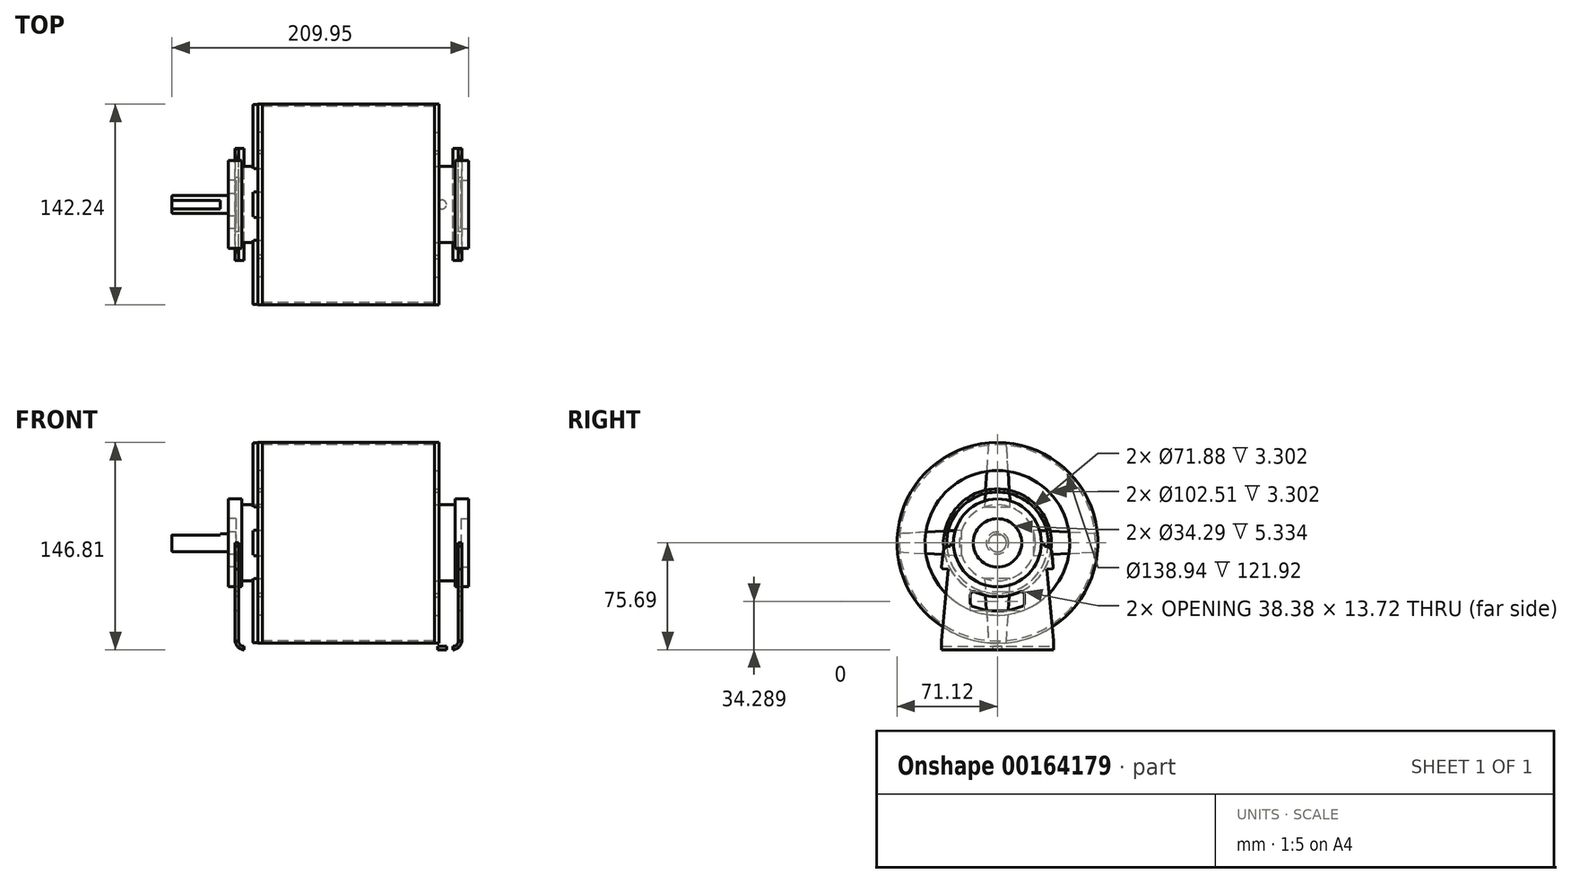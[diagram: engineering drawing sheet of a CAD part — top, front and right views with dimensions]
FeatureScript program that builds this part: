
annotation { "Feature Type Name" : "Feature", "Feature Type Description" : "" }
export const myFeature = defineFeature(function(context is Context, id is Id, definition is map)
    precondition{}
    {
        {
            var Q0;
            Q0=qCreatedBy(makeId("Right.planeOp"),FACE);
            var sketch = newSketch(context, id + "F0", { "sketchPlane" : qUnion([Q0])});
            skCircle(sketch, "E0", {"center": v(0, 0) * mm, "radius": 71.12 * mm});
            skCircle(sketch, "E1.0", {"center": v(0, 0) * mm, "radius": 69.47 * mm});
            skSolve(sketch);
        }
        {
            var Q0;
            Q0=makeQuery(id+"F0.imprint","IMPRINT",FACE,{"disambiguationData":[TD([[makeQuery(id+"F0.imprint","IMPRINT",EDGE,{"derivedFrom":sQuery(id+"F0.wireOp",EDGE,"E0")}),1.0]])]});
            extrude(context, id + "F1", {"entities" : qUnion([Q0]), "depth" : 121.92 * mm});
        }
        {
            var Q0;
            Q0=qCreatedBy(makeId("Front.planeOp"),FACE);
            var sketch = newSketch(context, id + "F2", { "sketchPlane" : qUnion([Q0])});
            skLineSegment(sketch, "E2", {"start": v(0, 0) * mm, "end": v(0, 71.12) * mm});
            skLineSegment(sketch, "E3", {"start": v(0, 71.12) * mm, "end": v(-3.3, 71.12) * mm});
            skLineSegment(sketch, "E4", {"start": v(-3.3, 71.12) * mm, "end": v(-3.3, 26.92) * mm});
            skLineSegment(sketch, "E5", {"start": v(-3.3, 26.92) * mm, "end": v(-14.48, 26.92) * mm});
            skLineSegment(sketch, "E6", {"start": v(-14.48, 26.92) * mm, "end": v(-14.48, 31.12) * mm});
            skLineSegment(sketch, "E7", {"start": v(-14.48, 31.12) * mm, "end": v(-24, 31.12) * mm});
            skLineSegment(sketch, "E8", {"start": v(-24, 31.12) * mm, "end": v(-24, 17.15) * mm});
            skLineSegment(sketch, "E9", {"start": v(-24, 17.15) * mm, "end": v(-18.67, 17.15) * mm});
            skLineSegment(sketch, "E10", {"start": v(-18.67, 17.15) * mm, "end": v(-18.67, 0) * mm});
            skLineSegment(sketch, "E11", {"start": v(-18.67, 0) * mm, "end": v(0, 0) * mm});
            skSolve(sketch);
        }
        {
            var Q0;
            Q0=makeQuery(id+"F2.imprint","IMPRINT",FACE,{"disambiguationData":[TD([[makeQuery(id+"F2.imprint","IMPRINT",EDGE,{"derivedFrom":sQuery(id+"F2.wireOp",EDGE,"E2")}),1.0]])]});
            var Q1;
            Q1=sQuery(id+"F2.wireOp",EDGE,"E11");
            revolve(context, id + "F3", {"entities" : qUnion([Q0]), "axis" : qUnion([Q1]), "revolveType" : RevolveType.FULL});
        }
        {
            var Q0;
            Q0=makeQuery(id+"F3.opRevolve","SWEPT_FACE",FACE,{"disambiguationData":[OSD([sQuery(id+"F2.wireOp",EDGE,"E4")])]});
            var sketch = newSketch(context, id + "F4", { "sketchPlane" : qUnion([Q0])});
            skCircle(sketch, "E12", {"center": v(0, 0) * mm, "radius": 51.26 * mm});
            skCircle(sketch, "E13", {"center": v(0, 0) * mm, "radius": 38.23 * mm});
            skCircle(sketch, "E14.0", {"center": v(0, 0) * mm, "radius": 35.94 * mm});
            skSolve(sketch);
        }
        {
            var Q0;
            Q0=qSketchRegion(id+"F4",true);
            var Q1;
            Q1=makeQuery(id+"F4.imprint","IMPRINT",FACE,{"disambiguationData":[TD([[makeQuery(id+"F4.imprint","IMPRINT",EDGE,{"derivedFrom":sQuery(id+"F4.wireOp",EDGE,"E14.0")}),1.0]])]});
            extrude(context, id + "F5", {"entities" : qUnion([Q0, Q1]), "operationType" : NewBodyOperationType.REMOVE, "endBound" : BoundingType.THROUGH_ALL, "oppositeDirection" : true, "depth" : 25.4 * mm});
        }
        {
            var Q0;
            Q0=qCreatedBy(makeId("Right.planeOp"),FACE);
            var sketch = newSketch(context, id + "F6", { "sketchPlane" : qUnion([Q0])});
            skLineSegment(sketch, "E15", {"start": v(0, 0) * mm, "end": v(0, 71.12) * mm, "construction": true});
            skPoint(sketch, "E16.rect.middle", {"position": v(0, 71.12) * mm});
            skCircle(sketch, "E17", {"center": v(0, 26.92) * mm, "radius": 9.2 * mm, "construction": true});
            skCircle(sketch, "E18.0", {"center": v(0, 0) * mm, "radius": 71.12 * mm, "construction": true});
            skCircle(sketch, "E19", {"center": v(0, 71.12) * mm, "radius": 6.35 * mm, "construction": true});
            skLineSegment(sketch, "E20", {"start": v(9.07, 25.35) * mm, "end": v(6.38, 70.83) * mm});
            skLineSegment(sketch, "E21", {"start": v(6.38, 70.83) * mm, "end": v(-6.38, 70.83) * mm});
            skLineSegment(sketch, "E22", {"start": v(-6.38, 70.83) * mm, "end": v(-9.07, 25.35) * mm});
            skLineSegment(sketch, "E23", {"start": v(-9.07, 25.35) * mm, "end": v(9.07, 25.35) * mm});
            skCircle(sketch, "E24.0", {"center": v(0, 0) * mm, "radius": 26.92 * mm, "construction": true});
            skSolve(sketch);
        }
        {
            var Q0;
            {var subQ3=sQuery(id+"F6.wireOp",EDGE,"E20");Q0=makeQuery(id+"F6.imprint","IMPRINT",FACE,{"disambiguationData":[TD([[makeQuery(id+"F6.imprint","IMPRINT",EDGE,{"derivedFrom":subQ3}),1.0]])]});}
            extrude(context, id + "F7", {"entities" : qUnion([Q0]), "oppositeDirection" : true, "depth" : 6.6 * mm});
        }
        {
            var Q0;
            Q0=makeQuery(id+"F7.opExtrude","CAP_EDGE",EDGE,{"disambiguationData":[OSD([sQuery(id+"F6.wireOp",EDGE,"E20")])],"isStart":false});
            var Q1;
            Q1=makeQuery(id+"F7.opExtrude","CAP_EDGE",EDGE,{"disambiguationData":[OSD([sQuery(id+"F6.wireOp",EDGE,"E21")])],"isStart":false});
            var Q2;
            Q2=makeQuery(id+"F7.opExtrude","CAP_EDGE",EDGE,{"disambiguationData":[OSD([sQuery(id+"F6.wireOp",EDGE,"E22")])],"isStart":false});
            var Q3;
            Q3=makeQuery(id+"F7.opExtrude","SWEPT_EDGE",EDGE,{"disambiguationData":[OSD([sQuery(id+"F2.wireOp",EDGE,"E3"),sQuery(id+"F2.wireOp",EDGE,"E4"),sQuery(id+"F6.wireOp",EDGE,"E20"),sQuery(id+"F6.wireOp",EDGE,"E21")])]});
            var Q4;
            Q4=makeQuery(id+"F7.opExtrude","SWEPT_EDGE",EDGE,{"disambiguationData":[OSD([sQuery(id+"F2.wireOp",EDGE,"E3"),sQuery(id+"F2.wireOp",EDGE,"E4"),sQuery(id+"F6.wireOp",EDGE,"E21"),sQuery(id+"F6.wireOp",EDGE,"E22")])]});
            fillet(context, id + "F8", {"entities" : qUnion([Q0, Q1, Q2, Q3, Q4]), "radius" : 0.5 * mm, "tangentPropagation" : true, "allowEdgeOverflow" : false});
        }
        {
            var Q0;
            Q0=makeQuery(id+"F7.opExtrude","SWEPT_BODY",BODY,{"disambiguationData":[OSD([sQuery(id+"F2.wireOp",EDGE,"E4"),sQuery(id+"F2.wireOp",EDGE,"E5"),sQuery(id+"F6.wireOp",EDGE,"E20"),sQuery(id+"F6.wireOp",EDGE,"E21"),sQuery(id+"F6.wireOp",EDGE,"E22")])]});
            var Q1;
            Q1=sQuery(id+"F2.wireOp",EDGE,"E11");
            circularPattern(context, id + "F9", {"entities" : qUnion([Q0]), "axis" : qUnion([Q1]), "angle" : 360 * degree, "instanceCount" : 4, "equalSpace" : true});
        }
        {
            var Q0;
            Q0=qCreatedBy(makeId("Right.planeOp"),FACE);
            cPlane(context, id + "F10", {"entities" : qUnion([Q0]), "cplaneType" : CPlaneType.OFFSET, "offset" : 60.96 * mm, "width" : 152.4 * mm, "height" : 152.4 * mm});
        }
        {
            var Q0;
            Q0=makeQuery(id+"F5.boolean.opBoolean","SPLIT",BODY,{"disambiguationData":[OD(0.0)],"derivedFrom":makeQuery(id+"F3.opRevolve","SWEPT_BODY",BODY,{"disambiguationData":[OSD([sQuery(id+"F2.wireOp",EDGE,"E2"),sQuery(id+"F2.wireOp",EDGE,"E3"),sQuery(id+"F2.wireOp",EDGE,"E4"),sQuery(id+"F2.wireOp",EDGE,"E5"),sQuery(id+"F2.wireOp",EDGE,"E6"),sQuery(id+"F2.wireOp",EDGE,"E7"),sQuery(id+"F2.wireOp",EDGE,"E8"),sQuery(id+"F2.wireOp",EDGE,"E9"),sQuery(id+"F2.wireOp",EDGE,"E10"),sQuery(id+"F2.wireOp",EDGE,"E11")])]})});
            var Q1;
            Q1=qCreatedBy(id+"F10.planeOp",FACE);
            mirror(context, id + "F11", {"entities" : qUnion([Q0]), "mirrorPlane" : qUnion([Q1])});
        }
        {
            var Q0;
            Q0=qCreatedBy(makeId("Front.planeOp"),FACE);
            var sketch = newSketch(context, id + "F12", { "sketchPlane" : qUnion([Q0])});
            skLineSegment(sketch, "E25.0.0", {"start": v(-18.67, -17.15) * mm, "end": v(-18.67, 17.15) * mm, "construction": true});
            skLineSegment(sketch, "E26", {"start": v(-18.67, 0) * mm, "end": v(-64.03, 0) * mm});
            skLineSegment(sketch, "E27", {"start": v(-64.03, 0) * mm, "end": v(-64.03, 5.84) * mm});
            skLineSegment(sketch, "E28", {"start": v(-63.53, 6.35) * mm, "end": v(-23.75, 6.35) * mm});
            skLineSegment(sketch, "E29", {"start": v(-23.24, 7.89) * mm, "end": v(-18.67, 7.89) * mm});
            skLineSegment(sketch, "E30", {"start": v(-18.67, 7.89) * mm, "end": v(-18.67, 0) * mm});
            skLineSegment(sketch, "E31", {"start": v(-23.75, 7.38) * mm, "end": v(-23.75, 6.35) * mm});
            skPoint(sketch, "E32.visualSharp", {"position": v(-23.75, 7.89) * mm});
            skArc(sketch, "E32.filletArc", {"start": v(-23.24, 7.89) * mm, "mid": v(-23.6, 7.74) * mm, "end": v(-23.75, 7.38) * mm});
            skPoint(sketch, "E33.visualSharp", {"position": v(-64.03, 6.35) * mm});
            skArc(sketch, "E33.filletArc", {"start": v(-63.53, 6.35) * mm, "mid": v(-63.88, 6.2) * mm, "end": v(-64.03, 5.84) * mm});
            skSolve(sketch);
        }
        {
            var Q0;
            Q0=makeQuery(id+"F12.imprint","IMPRINT",FACE,{"disambiguationData":[TD([[makeQuery(id+"F12.imprint","IMPRINT",EDGE,{"derivedFrom":sQuery(id+"F12.wireOp",EDGE,"E26")}),-1.0]])]});
            var Q1;
            Q1=sQuery(id+"F12.wireOp",EDGE,"E26");
            revolve(context, id + "F13", {"entities" : qUnion([Q0]), "axis" : qUnion([Q1]), "revolveType" : RevolveType.FULL});
        }
        {
            var Q0;
            Q0=makeQuery(id+"F13.opRevolve","SWEPT_FACE",FACE,{"disambiguationData":[OSD([sQuery(id+"F12.wireOp",EDGE,"E27")])]});
            var sketch = newSketch(context, id + "F14", { "sketchPlane" : qUnion([Q0])});
            skCircle(sketch, "E34.0", {"center": v(0, 0) * mm, "radius": 6.35 * mm});
            skLineSegment(sketch, "E35", {"start": v(-6.6, -6.35) * mm, "end": v(6.6, -6.35) * mm, "construction": true});
            skLineSegment(sketch, "E36", {"start": v(0, -6.35) * mm, "end": v(0, 6.35) * mm, "construction": true});
            skLineSegment(sketch, "E37.0", {"start": v(-3.02, 5.59) * mm, "end": v(3.02, 5.59) * mm});
            skSolve(sketch);
        }
        {
            var Q0;
            {var subQ0=makeQuery(id+"F13.opRevolve","SWEPT_EDGE",EDGE,{"disambiguationData":[OSD([sQuery(id+"F12.wireOp",EDGE,"E27"),sQuery(id+"F12.wireOp",EDGE,"E33.filletArc")])]});var subQ1=sQuery(id+"F14.wireOp",EDGE,"E37.0");var subQ3=makeQuery(id+"F14.imprint","INTERSECT",VERTEX,{"disambiguationData":[OD(0.0)],"derivedFrom":[subQ0,subQ1]});Q0=makeQuery(id+"F14.imprint","IMPRINT",FACE,{"disambiguationData":[TD([[makeQuery(id+"F14.imprint","IMPRINT",EDGE,{"disambiguationData":[TD([[subQ3,-1.0]])],"derivedFrom":subQ1}),1.0]])]});}
            var Q1;
            {var subQ1=sQuery(id+"F14.wireOp",EDGE,"E37.0");var subQ4=sQuery(id+"F14.wireOp",EDGE,"E34.0");var subQ6=makeQuery(id+"F14.imprint","INTERSECT",VERTEX,{"disambiguationData":[OD(0.0)],"derivedFrom":[subQ4,subQ1]});Q1=makeQuery(id+"F14.imprint","IMPRINT",FACE,{"disambiguationData":[TD([[makeQuery(id+"F14.imprint","IMPRINT",EDGE,{"disambiguationData":[TD([[subQ6,1.0]])],"derivedFrom":subQ4}),1.0]])]});}
            extrude(context, id + "F15", {"entities" : qUnion([Q0, Q1]), "operationType" : NewBodyOperationType.REMOVE, "oppositeDirection" : true, "depth" : 34.04 * mm});
        }
        {
            var Q0;
            Q0=qCreatedBy(makeId("Front.planeOp"),FACE);
            var sketch = newSketch(context, id + "F16", { "sketchPlane" : qUnion([Q0])});
            skLineSegment(sketch, "E38", {"start": v(-154.25, 0) * mm, "end": v(252.33, 0) * mm, "construction": true});
            skLineSegment(sketch, "E39", {"start": v(-12.9, -75.7) * mm, "end": v(134.81, -75.7) * mm});
            skLineSegment(sketch, "E40", {"start": v(-24, 31.12) * mm, "end": v(-14.48, 31.12) * mm, "construction": true});
            skLineSegment(sketch, "E41", {"start": v(136.4, 31.12) * mm, "end": v(145.92, 31.12) * mm, "construction": true});
            skLineSegment(sketch, "E42", {"start": v(-19.24, 31.12) * mm, "end": v(-19.24, 0) * mm, "construction": true});
            skLineSegment(sketch, "E43", {"start": v(141.16, 31.12) * mm, "end": v(141.16, 0) * mm, "construction": true});
            skLineSegment(sketch, "E44", {"start": v(-19.24, 0) * mm, "end": v(-19.24, -69.34) * mm});
            skLineSegment(sketch, "E45", {"start": v(141.16, 0) * mm, "end": v(141.16, -69.34) * mm});
            skPoint(sketch, "E46.visualSharp", {"position": v(-19.24, -75.7) * mm});
            skArc(sketch, "E46.filletArc", {"start": v(-19.24, -69.34) * mm, "mid": v(-17.38, -73.83) * mm, "end": v(-12.9, -75.7) * mm});
            skPoint(sketch, "E47.visualSharp", {"position": v(141.16, -75.7) * mm});
            skArc(sketch, "E47.filletArc", {"start": v(134.81, -75.7) * mm, "mid": v(139.3, -73.83) * mm, "end": v(141.16, -69.34) * mm});
            skLineSegment(sketch, "E48.0", {"start": v(138.87, 0) * mm, "end": v(138.87, -69.34) * mm});
            skArc(sketch, "E48.1", {"start": v(134.81, -73.4) * mm, "mid": v(137.68, -72.22) * mm, "end": v(138.87, -69.34) * mm});
            skLineSegment(sketch, "E48.2", {"start": v(-12.9, -73.4) * mm, "end": v(134.81, -73.4) * mm});
            skArc(sketch, "E48.3", {"start": v(-16.95, -69.34) * mm, "mid": v(-15.76, -72.22) * mm, "end": v(-12.9, -73.4) * mm});
            skLineSegment(sketch, "E48.4", {"start": v(-16.95, 0) * mm, "end": v(-16.95, -69.34) * mm});
            skLineSegment(sketch, "E49", {"start": v(-19.24, 0) * mm, "end": v(-16.95, 0) * mm});
            skLineSegment(sketch, "E50", {"start": v(138.87, 0) * mm, "end": v(141.16, 0) * mm});
            skSolve(sketch);
        }
        {
            var Q0;
            Q0=qSketchRegion(id+"F16",true);
            extrude(context, id + "F17", {"entities" : qUnion([Q0]), "depth" : 79.5 * mm, "symmetric" : true});
        }
        {
            var Q0;
            Q0=qCreatedBy(makeId("Top.planeOp"),FACE);
            cPlane(context, id + "F18", {"entities" : qUnion([Q0]), "cplaneType" : CPlaneType.OFFSET, "offset" : 75.7 * mm, "oppositeDirection" : true, "width" : 152.4 * mm, "height" : 152.4 * mm});
        }
        {
            var Q0;
            Q0=qCreatedBy(id+"F18.planeOp",FACE);
            var sketch = newSketch(context, id + "F19", { "sketchPlane" : qUnion([Q0])});
            skLineSegment(sketch, "E51.0", {"start": v(-19.24, -39.75) * mm, "end": v(-12.9, -39.75) * mm, "construction": true});
            skLineSegment(sketch, "E52.0", {"start": v(-19.24, 39.75) * mm, "end": v(-12.9, 39.75) * mm, "construction": true});
            skLineSegment(sketch, "E53.bottom", {"start": v(15.34, 66.04) * mm, "end": v(15.34, 66.04) * mm});
            skLineSegment(sketch, "E53.top", {"start": v(15.34, 40.64) * mm, "end": v(15.34, 40.64) * mm});
            skLineSegment(sketch, "E53.left", {"start": v(11.37, 62.07) * mm, "end": v(11.37, 44.6) * mm});
            skLineSegment(sketch, "E53.right", {"start": v(19.3, 62.07) * mm, "end": v(19.3, 44.6) * mm});
            skPoint(sketch, "E54.visualSharp", {"position": v(11.37, 66.04) * mm});
            skArc(sketch, "E54.filletArc", {"start": v(15.34, 66.04) * mm, "mid": v(12.53, 64.88) * mm, "end": v(11.37, 62.07) * mm});
            skPoint(sketch, "E55.visualSharp", {"position": v(19.3, 66.04) * mm});
            skArc(sketch, "E55.filletArc", {"start": v(19.3, 62.07) * mm, "mid": v(18.14, 64.88) * mm, "end": v(15.34, 66.04) * mm});
            skPoint(sketch, "E56.visualSharp", {"position": v(19.3, 40.64) * mm});
            skArc(sketch, "E56.filletArc", {"start": v(15.34, 40.64) * mm, "mid": v(18.14, 41.8) * mm, "end": v(19.3, 44.6) * mm});
            skPoint(sketch, "E57.visualSharp", {"position": v(11.37, 40.64) * mm});
            skArc(sketch, "E57.filletArc", {"start": v(11.37, 44.6) * mm, "mid": v(12.53, 41.8) * mm, "end": v(15.34, 40.64) * mm});
            skLineSegment(sketch, "E58", {"start": v(2.98, 39.75) * mm, "end": v(2.98, -39.75) * mm, "construction": true});
            skLineSegment(sketch, "E59", {"start": v(-19.24, 0) * mm, "end": v(141.16, 0) * mm, "construction": true});
            skLineSegment(sketch, "E60", {"start": v(9.33, 71.5) * mm, "end": v(111.68, 71.5) * mm});
            skLineSegment(sketch, "E61", {"start": v(9.33, -71.5) * mm, "end": v(111.68, -71.5) * mm});
            skLineSegment(sketch, "E62", {"start": v(2.98, 46.1) * mm, "end": v(2.98, 65.15) * mm});
            skLineSegment(sketch, "E63", {"start": v(2.98, -46.1) * mm, "end": v(2.98, -65.15) * mm});
            skLineSegment(sketch, "E64", {"start": v(-19.24, 39.75) * mm, "end": v(-19.24, -39.75) * mm, "construction": true});
            skLineSegment(sketch, "E65.0", {"start": v(141.16, -39.75) * mm, "end": v(141.16, 39.75) * mm, "construction": true});
            skLineSegment(sketch, "E66", {"start": v(141.16, 39.75) * mm, "end": v(134.81, 39.75) * mm, "construction": true});
            skLineSegment(sketch, "E67", {"start": v(126.25, 45.4) * mm, "end": v(117.6, 67.47) * mm});
            skPoint(sketch, "E68.visualSharp", {"position": v(128.46, 39.75) * mm});
            skArc(sketch, "E68.filletArc", {"start": v(126.25, 45.4) * mm, "mid": v(129.51, 41.3) * mm, "end": v(134.52, 39.75) * mm});
            skPoint(sketch, "E69.visualSharp", {"position": v(2.98, 71.5) * mm});
            skArc(sketch, "E69.filletArc", {"start": v(9.33, 71.5) * mm, "mid": v(4.84, 69.64) * mm, "end": v(2.98, 65.15) * mm});
            skLineSegment(sketch, "E70.0.MirrorCS", {"start": v(141.16, -39.75) * mm, "end": v(134.81, -39.75) * mm, "construction": true});
            skLineSegment(sketch, "E70.1.MirrorCS", {"start": v(126.25, -45.4) * mm, "end": v(117.6, -67.47) * mm});
            skArc(sketch, "E70.2.MirrorCS", {"start": v(126.25, -45.4) * mm, "mid": v(129.51, -41.3) * mm, "end": v(134.52, -39.75) * mm});
            skPoint(sketch, "E71.visualSharp", {"position": v(116.01, 71.5) * mm});
            skArc(sketch, "E71.filletArc", {"start": v(117.6, 67.47) * mm, "mid": v(115.26, 70.4) * mm, "end": v(111.68, 71.5) * mm});
            skPoint(sketch, "E72.visualSharp", {"position": v(116.01, -71.5) * mm});
            skArc(sketch, "E72.filletArc", {"start": v(111.68, -71.5) * mm, "mid": v(115.26, -70.4) * mm, "end": v(117.6, -67.47) * mm});
            skPoint(sketch, "E73.visualSharp", {"position": v(2.98, -71.5) * mm});
            skArc(sketch, "E73.filletArc", {"start": v(2.98, -65.15) * mm, "mid": v(4.84, -69.64) * mm, "end": v(9.33, -71.5) * mm});
            skPoint(sketch, "E74.visualSharp", {"position": v(2.98, 39.75) * mm});
            skArc(sketch, "E74.filletArc", {"start": v(-3.37, 39.75) * mm, "mid": v(1.12, 41.61) * mm, "end": v(2.98, 46.1) * mm});
            skPoint(sketch, "E75.visualSharp", {"position": v(2.98, -39.75) * mm});
            skArc(sketch, "E75.filletArc", {"start": v(2.98, -46.1) * mm, "mid": v(1.12, -41.61) * mm, "end": v(-3.37, -39.75) * mm});
            skArc(sketch, "E76.0.1.0", {"start": v(15.34, -66.04) * mm, "mid": v(18.14, -64.88) * mm, "end": v(19.3, -62.07) * mm});
            skArc(sketch, "E76.0.1.1", {"start": v(11.37, -62.07) * mm, "mid": v(12.53, -64.88) * mm, "end": v(15.34, -66.04) * mm});
            skLineSegment(sketch, "E76.0.1.2", {"start": v(11.37, -44.6) * mm, "end": v(11.37, -62.07) * mm});
            skArc(sketch, "E76.0.1.3", {"start": v(15.34, -40.64) * mm, "mid": v(12.53, -41.8) * mm, "end": v(11.37, -44.6) * mm});
            skArc(sketch, "E76.0.1.4", {"start": v(19.3, -44.6) * mm, "mid": v(18.14, -41.8) * mm, "end": v(15.34, -40.64) * mm});
            skLineSegment(sketch, "E76.0.1.5", {"start": v(19.3, -44.6) * mm, "end": v(19.3, -62.07) * mm});
            skArc(sketch, "E76.1.0.0", {"start": v(83.92, 40.64) * mm, "mid": v(86.72, 41.8) * mm, "end": v(87.88, 44.6) * mm});
            skArc(sketch, "E76.1.0.1", {"start": v(79.95, 44.6) * mm, "mid": v(81.1, 41.8) * mm, "end": v(83.92, 40.64) * mm});
            skLineSegment(sketch, "E76.1.0.2", {"start": v(79.95, 62.07) * mm, "end": v(79.95, 44.6) * mm});
            skArc(sketch, "E76.1.0.3", {"start": v(83.92, 66.04) * mm, "mid": v(81.1, 64.88) * mm, "end": v(79.95, 62.07) * mm});
            skArc(sketch, "E76.1.0.4", {"start": v(87.88, 62.07) * mm, "mid": v(86.72, 64.88) * mm, "end": v(83.92, 66.04) * mm});
            skLineSegment(sketch, "E76.1.0.5", {"start": v(87.88, 62.07) * mm, "end": v(87.88, 44.6) * mm});
            skArc(sketch, "E76.1.1.0", {"start": v(83.92, -66.04) * mm, "mid": v(86.72, -64.88) * mm, "end": v(87.88, -62.07) * mm});
            skArc(sketch, "E76.1.1.1", {"start": v(79.95, -62.07) * mm, "mid": v(81.1, -64.88) * mm, "end": v(83.92, -66.04) * mm});
            skLineSegment(sketch, "E76.1.1.2", {"start": v(79.95, -44.6) * mm, "end": v(79.95, -62.07) * mm});
            skArc(sketch, "E76.1.1.3", {"start": v(83.92, -40.64) * mm, "mid": v(81.1, -41.8) * mm, "end": v(79.95, -44.6) * mm});
            skArc(sketch, "E76.1.1.4", {"start": v(87.88, -44.6) * mm, "mid": v(86.72, -41.8) * mm, "end": v(83.92, -40.64) * mm});
            skLineSegment(sketch, "E76.1.1.5", {"start": v(87.88, -44.6) * mm, "end": v(87.88, -62.07) * mm});
            skLineSegment(sketch, "E76.direction1", {"start": v(15.34, 40.64) * mm, "end": v(83.92, 40.64) * mm, "construction": true});
            skLineSegment(sketch, "E76.direction2", {"start": v(15.34, 40.64) * mm, "end": v(15.34, -66.04) * mm, "construction": true});
            skLineSegment(sketch, "E77.0", {"start": v(-12.9, -39.75) * mm, "end": v(-12.9, 39.75) * mm});
            skLineSegment(sketch, "E78.0", {"start": v(134.81, -39.75) * mm, "end": v(134.81, 39.75) * mm});
            skLineSegment(sketch, "E79", {"start": v(-12.9, 39.75) * mm, "end": v(-3.37, 39.75) * mm});
            skLineSegment(sketch, "E80", {"start": v(-12.9, -39.75) * mm, "end": v(-3.37, -39.75) * mm});
            skLineSegment(sketch, "E81", {"start": v(134.81, 39.75) * mm, "end": v(134.52, 39.75) * mm});
            skLineSegment(sketch, "E82", {"start": v(134.81, -39.75) * mm, "end": v(134.52, -39.75) * mm});
            skSolve(sketch);
        }
        {
            var Q0;
            Q0=makeQuery(id+"F19.imprint","IMPRINT",FACE,{"disambiguationData":[TD([[makeQuery(id+"F19.imprint","IMPRINT",EDGE,{"derivedFrom":sQuery(id+"F19.wireOp",EDGE,"E53.left")}),-1.0]])]});
            extrude(context, id + "F20", {"entities" : qUnion([Q0]), "operationType" : NewBodyOperationType.ADD, "depth" : 2.3 * mm});
        }
        {
            var Q0;
            Q0=makeQuery(id+"F17.opExtrude","SWEPT_FACE",FACE,{"disambiguationData":[OSD([sQuery(id+"F16.wireOp",EDGE,"E44")])]});
            var sketch = newSketch(context, id + "F21", { "sketchPlane" : qUnion([Q0])});
            skArc(sketch, "E83.0", {"start": v(-31.12, 0) * mm, "mid": v(0, -31.12) * mm, "end": v(31.12, 0) * mm});
            skLineSegment(sketch, "E84.0", {"start": v(39.75, -69.34) * mm, "end": v(-39.75, -69.34) * mm});
            skLineSegment(sketch, "E85", {"start": v(31.87, 0) * mm, "end": v(31.12, 0) * mm});
            skLineSegment(sketch, "E86", {"start": v(-33.13, -1.15) * mm, "end": v(-39.75, -69.34) * mm});
            skLineSegment(sketch, "E87", {"start": v(33.13, -1.15) * mm, "end": v(39.75, -69.34) * mm});
            skPoint(sketch, "E88.end.orphan", {"position": v(-39.75, 0) * mm});
            skPoint(sketch, "E89.0.start.orphan", {"position": v(39.75, 0) * mm});
            skLineSegment(sketch, "E90.trimOffspring", {"start": v(-31.12, 0) * mm, "end": v(-31.87, 0) * mm});
            skLineSegment(sketch, "E91", {"start": v(0, 0) * mm, "end": v(0, -69.34) * mm, "construction": true});
            skPoint(sketch, "E92.visualSharp", {"position": v(-33.02, 0) * mm});
            skArc(sketch, "E92.filletArc", {"start": v(-31.87, 0) * mm, "mid": v(-32.72, -0.33) * mm, "end": v(-33.13, -1.15) * mm});
            skPoint(sketch, "E93.visualSharp", {"position": v(33.02, 0) * mm});
            skArc(sketch, "E93.filletArc", {"start": v(33.13, -1.15) * mm, "mid": v(32.72, -0.33) * mm, "end": v(31.87, 0) * mm});
            skLineSegment(sketch, "E94.bottom", {"start": v(33.27, -2.6) * mm, "end": v(33.78, -2.55) * mm});
            skLineSegment(sketch, "E94.top", {"start": v(34.84, -18.78) * mm, "end": v(38.38, -18.44) * mm});
            skLineSegment(sketch, "E94.left", {"start": v(33.27, -2.6) * mm, "end": v(34.84, -18.78) * mm});
            skLineSegment(sketch, "E94.right", {"start": v(38.5, -6.43) * mm, "end": v(39.52, -17.05) * mm});
            skPoint(sketch, "E95.visualSharp", {"position": v(38.08, -2.13) * mm});
            skArc(sketch, "E95.filletArc", {"start": v(38.5, -6.43) * mm, "mid": v(36.94, -3.51) * mm, "end": v(33.78, -2.55) * mm});
            skPoint(sketch, "E96.visualSharp", {"position": v(39.65, -18.31) * mm});
            skArc(sketch, "E96.filletArc", {"start": v(38.38, -18.44) * mm, "mid": v(39.24, -17.98) * mm, "end": v(39.52, -17.05) * mm});
            skLineSegment(sketch, "E97.0.MirrorCS", {"start": v(-33.27, -2.6) * mm, "end": v(-33.78, -2.55) * mm});
            skArc(sketch, "E97.1.MirrorCS", {"start": v(-38.5, -6.43) * mm, "mid": v(-36.94, -3.51) * mm, "end": v(-33.78, -2.55) * mm});
            skLineSegment(sketch, "E97.2.MirrorCS", {"start": v(-34.84, -18.78) * mm, "end": v(-38.38, -18.44) * mm});
            skLineSegment(sketch, "E97.3.MirrorCS", {"start": v(-38.5, -6.43) * mm, "end": v(-39.52, -17.05) * mm});
            skArc(sketch, "E97.4.MirrorCS", {"start": v(-38.38, -18.44) * mm, "mid": v(-39.24, -17.98) * mm, "end": v(-39.52, -17.05) * mm});
            skArc(sketch, "E98", {"start": v(-15.6, -34.76) * mm, "mid": v(0, -38.1) * mm, "end": v(15.6, -34.76) * mm});
            skArc(sketch, "E99.0", {"start": v(-17.57, -44.95) * mm, "mid": v(0, -48.26) * mm, "end": v(17.57, -44.95) * mm});
            skLineSegment(sketch, "E100.rect.left", {"start": v(19.19, -37.07) * mm, "end": v(19.19, -42.58) * mm});
            skLineSegment(sketch, "E100.rect.right", {"start": v(-19.19, -37.07) * mm, "end": v(-19.19, -42.58) * mm});
            skPoint(sketch, "E100.rect.middle", {"position": v(0, -43.18) * mm});
            skPoint(sketch, "E101.orphan", {"position": v(-19.19, -53.44) * mm});
            skPoint(sketch, "E100.rect.top.start.orphan", {"position": v(19.19, -53.44) * mm});
            skPoint(sketch, "E102.visualSharp", {"position": v(-19.19, -44.28) * mm});
            skArc(sketch, "E102.filletArc", {"start": v(-19.19, -42.58) * mm, "mid": v(-18.75, -44.01) * mm, "end": v(-17.57, -44.95) * mm});
            skPoint(sketch, "E103.visualSharp", {"position": v(19.19, -44.28) * mm});
            skArc(sketch, "E103.filletArc", {"start": v(17.57, -44.95) * mm, "mid": v(18.75, -44.01) * mm, "end": v(19.19, -42.58) * mm});
            skPoint(sketch, "E104.visualSharp", {"position": v(19.19, -32.92) * mm});
            skArc(sketch, "E104.filletArc", {"start": v(19.19, -37.07) * mm, "mid": v(18.03, -34.94) * mm, "end": v(15.6, -34.76) * mm});
            skPoint(sketch, "E105.visualSharp", {"position": v(-19.19, -32.92) * mm});
            skArc(sketch, "E105.filletArc", {"start": v(-15.6, -34.76) * mm, "mid": v(-18.03, -34.94) * mm, "end": v(-19.19, -37.07) * mm});
            skSolve(sketch);
        }
        {
            var Q0;
            {var subQ2=sQuery(id+"F21.wireOp",EDGE,"E92.filletArc");Q0=makeQuery(id+"F21.imprint","IMPRINT",FACE,{"disambiguationData":[TD([[makeQuery(id+"F21.imprint","IMPRINT",EDGE,{"derivedFrom":subQ2}),-1.0]])]});}
            var Q1;
            {var subQ2=sQuery(id+"F21.wireOp",EDGE,"E93.filletArc");Q1=makeQuery(id+"F21.imprint","IMPRINT",FACE,{"disambiguationData":[TD([[makeQuery(id+"F21.imprint","IMPRINT",EDGE,{"derivedFrom":subQ2}),-1.0]])]});}
            var Q2;
            {var subQ1=sQuery(id+"F21.wireOp",EDGE,"E83.0");Q2=makeQuery(id+"F21.imprint","IMPRINT",FACE,{"disambiguationData":[TD([[makeQuery(id+"F21.imprint","IMPRINT",EDGE,{"derivedFrom":subQ1}),1.0]])]});}
            var Q3;
            Q3=makeQuery(id+"F21.imprint","IMPRINT",FACE,{"disambiguationData":[TD([[makeQuery(id+"F21.imprint","IMPRINT",EDGE,{"derivedFrom":sQuery(id+"F21.wireOp",EDGE,"E98")}),-1.0]])]});
            extrude(context, id + "F22", {"entities" : qUnion([Q0, Q1, Q2, Q3]), "oppositeDirection" : true, "depth" : 160.4 * mm});
        }
        {
            var Q0;
            Q0=makeQuery(id+"F22.opExtrude","SWEPT_BODY",BODY,{"disambiguationData":[OSD([sQuery(id+"F16.wireOp",EDGE,"E44"),sQuery(id+"F16.wireOp",EDGE,"E49"),sQuery(id+"F21.wireOp",EDGE,"E83.0")])]});
            var Q1;
            Q1=makeQuery(id+"F22.opExtrude","SWEPT_BODY",BODY,{"disambiguationData":[OSD([sQuery(id+"F16.wireOp",EDGE,"E44"),sQuery(id+"F16.wireOp",EDGE,"E49"),sQuery(id+"F21.wireOp",EDGE,"E86"),sQuery(id+"F21.wireOp",EDGE,"E92.filletArc"),sQuery(id+"F21.wireOp",EDGE,"E97.0.MirrorCS"),sQuery(id+"F21.wireOp",EDGE,"E97.1.MirrorCS"),sQuery(id+"F21.wireOp",EDGE,"E97.2.MirrorCS"),sQuery(id+"F21.wireOp",EDGE,"E97.3.MirrorCS"),sQuery(id+"F21.wireOp",EDGE,"E97.4.MirrorCS")])]});
            var Q2;
            Q2=makeQuery(id+"F22.opExtrude","SWEPT_BODY",BODY,{"disambiguationData":[OSD([sQuery(id+"F16.wireOp",EDGE,"E44"),sQuery(id+"F16.wireOp",EDGE,"E49"),sQuery(id+"F21.wireOp",EDGE,"E87"),sQuery(id+"F21.wireOp",EDGE,"E93.filletArc"),sQuery(id+"F21.wireOp",EDGE,"E94.bottom"),sQuery(id+"F21.wireOp",EDGE,"E94.top"),sQuery(id+"F21.wireOp",EDGE,"E94.right"),sQuery(id+"F21.wireOp",EDGE,"E95.filletArc"),sQuery(id+"F21.wireOp",EDGE,"E96.filletArc")])]});
            var Q3;
            Q3=makeQuery(id+"F22.opExtrude","SWEPT_BODY",BODY,{"disambiguationData":[OSD([sQuery(id+"F21.wireOp",EDGE,"E98"),sQuery(id+"F21.wireOp",EDGE,"E99.0"),sQuery(id+"F21.wireOp",EDGE,"E100.rect.left"),sQuery(id+"F21.wireOp",EDGE,"E100.rect.right"),sQuery(id+"F21.wireOp",EDGE,"E102.filletArc"),sQuery(id+"F21.wireOp",EDGE,"E103.filletArc"),sQuery(id+"F21.wireOp",EDGE,"E104.filletArc"),sQuery(id+"F21.wireOp",EDGE,"E105.filletArc")])]});
            var Q4;
            Q4=makeQuery(id+"F17.opExtrude","SWEPT_BODY",BODY,{"disambiguationData":[OSD([sQuery(id+"F16.wireOp",EDGE,"E39"),sQuery(id+"F16.wireOp",EDGE,"E44"),sQuery(id+"F16.wireOp",EDGE,"E45"),sQuery(id+"F16.wireOp",EDGE,"E46.filletArc"),sQuery(id+"F16.wireOp",EDGE,"E47.filletArc"),sQuery(id+"F16.wireOp",EDGE,"E48.0"),sQuery(id+"F16.wireOp",EDGE,"E48.1"),sQuery(id+"F16.wireOp",EDGE,"E48.2"),sQuery(id+"F16.wireOp",EDGE,"E48.3"),sQuery(id+"F16.wireOp",EDGE,"E48.4"),sQuery(id+"F16.wireOp",EDGE,"E49"),sQuery(id+"F16.wireOp",EDGE,"E50")])]});
            booleanBodies(context, id + "F23", {"operationType" : BooleanOperationType.SUBTRACTION, "tools" : qUnion([Q0, Q1, Q2, Q3]), "targets" : qUnion([Q4])});
        }
        {
            var Q0;
            Q0=makeQuery(id+"F20.boolean.opBoolean","MERGE",FACE,{"derivedFrom":[makeQuery(id+"F17.opExtrude","SWEPT_FACE",FACE,{"disambiguationData":[OSD([sQuery(id+"F16.wireOp",EDGE,"E48.2")])]}),makeQuery(id+"F20.opExtrude","CAP_FACE",FACE,{"disambiguationData":[OSD([sQuery(id+"F19.wireOp",EDGE,"E53.left"),sQuery(id+"F19.wireOp",EDGE,"E53.right"),sQuery(id+"F19.wireOp",EDGE,"E54.filletArc"),sQuery(id+"F19.wireOp",EDGE,"E55.filletArc"),sQuery(id+"F19.wireOp",EDGE,"E56.filletArc"),sQuery(id+"F19.wireOp",EDGE,"E57.filletArc"),sQuery(id+"F19.wireOp",EDGE,"E60"),sQuery(id+"F19.wireOp",EDGE,"E61"),sQuery(id+"F19.wireOp",EDGE,"E62"),sQuery(id+"F19.wireOp",EDGE,"E63"),sQuery(id+"F19.wireOp",EDGE,"E67"),sQuery(id+"F19.wireOp",EDGE,"E68.filletArc"),sQuery(id+"F19.wireOp",EDGE,"E69.filletArc"),sQuery(id+"F19.wireOp",EDGE,"E70.1.MirrorCS"),sQuery(id+"F19.wireOp",EDGE,"E70.2.MirrorCS"),sQuery(id+"F19.wireOp",EDGE,"E71.filletArc"),sQuery(id+"F19.wireOp",EDGE,"E72.filletArc"),sQuery(id+"F19.wireOp",EDGE,"E73.filletArc"),sQuery(id+"F19.wireOp",EDGE,"E74.filletArc"),sQuery(id+"F19.wireOp",EDGE,"E75.filletArc"),sQuery(id+"F19.wireOp",EDGE,"E76.0.1.0"),sQuery(id+"F19.wireOp",EDGE,"E76.0.1.1"),sQuery(id+"F19.wireOp",EDGE,"E76.0.1.2"),sQuery(id+"F19.wireOp",EDGE,"E76.0.1.3"),sQuery(id+"F19.wireOp",EDGE,"E76.0.1.4"),sQuery(id+"F19.wireOp",EDGE,"E76.0.1.5"),sQuery(id+"F19.wireOp",EDGE,"E76.1.0.0"),sQuery(id+"F19.wireOp",EDGE,"E76.1.0.1"),sQuery(id+"F19.wireOp",EDGE,"E76.1.0.2"),sQuery(id+"F19.wireOp",EDGE,"E76.1.0.3"),sQuery(id+"F19.wireOp",EDGE,"E76.1.0.4"),sQuery(id+"F19.wireOp",EDGE,"E76.1.0.5"),sQuery(id+"F19.wireOp",EDGE,"E76.1.1.0"),sQuery(id+"F19.wireOp",EDGE,"E76.1.1.1"),sQuery(id+"F19.wireOp",EDGE,"E76.1.1.2"),sQuery(id+"F19.wireOp",EDGE,"E76.1.1.3"),sQuery(id+"F19.wireOp",EDGE,"E76.1.1.4"),sQuery(id+"F19.wireOp",EDGE,"E76.1.1.5"),sQuery(id+"F19.wireOp",EDGE,"E77.0"),sQuery(id+"F19.wireOp",EDGE,"E78.0"),sQuery(id+"F19.wireOp",EDGE,"E79"),sQuery(id+"F19.wireOp",EDGE,"E80"),sQuery(id+"F19.wireOp",EDGE,"E81"),sQuery(id+"F19.wireOp",EDGE,"E82")])],"isStart":false})]});
            var sketch = newSketch(context, id + "F24", { "sketchPlane" : qUnion([Q0])});
            skLineSegment(sketch, "E106.0", {"start": v(-12.9, -39.75) * mm, "end": v(-12.9, 39.75) * mm, "construction": true});
            skLineSegment(sketch, "E107.0", {"start": v(134.81, -39.75) * mm, "end": v(134.81, 39.75) * mm, "construction": true});
            skLineSegment(sketch, "E108.rect.bottom", {"start": v(4.89, 7.62) * mm, "end": v(117.03, 7.62) * mm});
            skLineSegment(sketch, "E108.rect.top", {"start": v(4.89, -7.62) * mm, "end": v(117.03, -7.62) * mm});
            skLineSegment(sketch, "E108.rect.left", {"start": v(2.35, 5.08) * mm, "end": v(2.35, -5.08) * mm});
            skLineSegment(sketch, "E108.rect.right", {"start": v(119.57, 5.08) * mm, "end": v(119.57, -5.08) * mm});
            skPoint(sketch, "E108.rect.middle", {"position": v(60.96, 0) * mm});
            skLineSegment(sketch, "E109", {"start": v(2.35, 0) * mm, "end": v(-12.9, 0) * mm, "construction": true});
            skLineSegment(sketch, "E110", {"start": v(119.57, 0) * mm, "end": v(134.81, 0) * mm, "construction": true});
            skCircle(sketch, "E111", {"center": v(-5.27, 0) * mm, "radius": 3.18 * mm});
            skLineSegment(sketch, "E112", {"start": v(60.96, 7.62) * mm, "end": v(60.96, -7.62) * mm, "construction": true});
            skCircle(sketch, "E113.0.MirrorC", {"center": v(127.2, 0) * mm, "radius": 3.18 * mm});
            skPoint(sketch, "E114.visualSharp", {"position": v(2.35, 7.62) * mm});
            skArc(sketch, "E114.filletArc", {"start": v(4.89, 7.62) * mm, "mid": v(3.1, 6.88) * mm, "end": v(2.35, 5.08) * mm});
            skPoint(sketch, "E115.visualSharp", {"position": v(119.57, 7.62) * mm});
            skArc(sketch, "E115.filletArc", {"start": v(119.57, 5.08) * mm, "mid": v(118.83, 6.88) * mm, "end": v(117.03, 7.62) * mm});
            skPoint(sketch, "E116.visualSharp", {"position": v(119.57, -7.62) * mm});
            skArc(sketch, "E116.filletArc", {"start": v(117.03, -7.62) * mm, "mid": v(118.83, -6.88) * mm, "end": v(119.57, -5.08) * mm});
            skPoint(sketch, "E117.visualSharp", {"position": v(2.35, -7.62) * mm});
            skArc(sketch, "E117.filletArc", {"start": v(2.35, -5.08) * mm, "mid": v(3.1, -6.88) * mm, "end": v(4.89, -7.62) * mm});
            skSolve(sketch);
        }
        {
            var Q0;
            Q0=makeQuery(id+"F24.imprint","IMPRINT",FACE,{"disambiguationData":[TD([[makeQuery(id+"F24.imprint","IMPRINT",EDGE,{"derivedFrom":sQuery(id+"F24.wireOp",EDGE,"E111")}),1.0]])]});
            var Q1;
            Q1=makeQuery(id+"F24.imprint","IMPRINT",FACE,{"disambiguationData":[TD([[makeQuery(id+"F24.imprint","IMPRINT",EDGE,{"derivedFrom":sQuery(id+"F24.wireOp",EDGE,"E108.rect.bottom")}),-1.0]])]});
            var Q2;
            Q2=makeQuery(id+"F24.imprint","IMPRINT",FACE,{"disambiguationData":[TD([[makeQuery(id+"F24.imprint","IMPRINT",EDGE,{"derivedFrom":sQuery(id+"F24.wireOp",EDGE,"E113.0.MirrorC")}),-1.0]])]});
            extrude(context, id + "F25", {"entities" : qUnion([Q0, Q1, Q2]), "operationType" : NewBodyOperationType.REMOVE, "endBound" : BoundingType.THROUGH_ALL, "oppositeDirection" : true, "depth" : 25.4 * mm});
        }
    });
